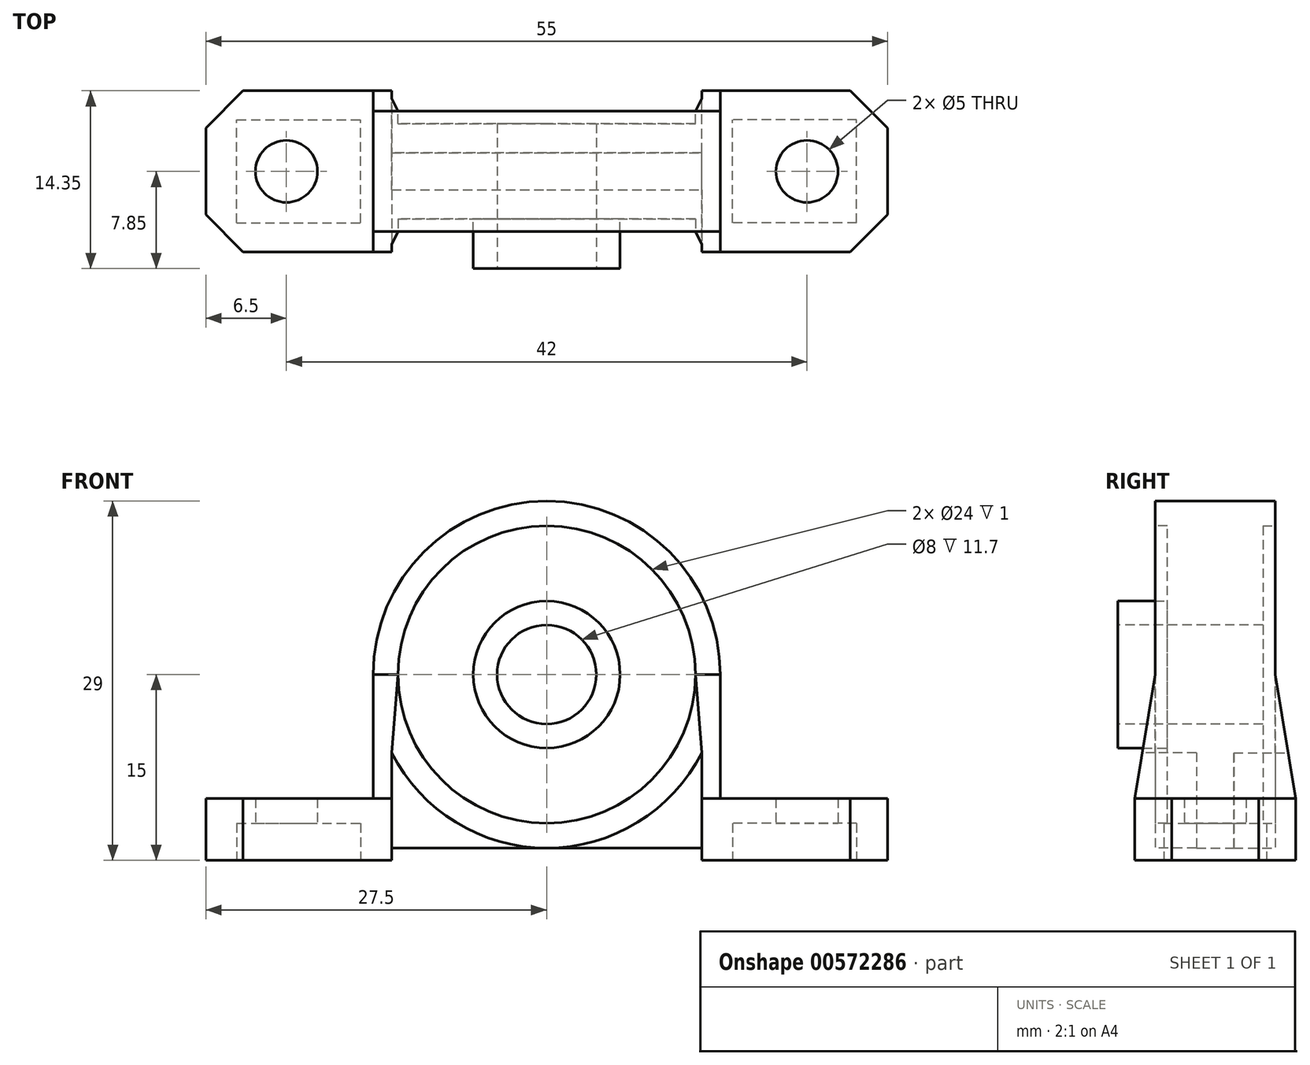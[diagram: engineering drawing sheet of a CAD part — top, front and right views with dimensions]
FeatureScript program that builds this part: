
annotation { "Feature Type Name" : "Feature", "Feature Type Description" : "" }
export const myFeature = defineFeature(function(context is Context, id is Id, definition is map)
    precondition{}
    {
        {
            var Q0;
            Q0=qCreatedBy(makeId("Top.planeOp"),FACE);
            var sketch = newSketch(context, id + "F0", { "sketchPlane" : qUnion([Q0])});
            skLineSegment(sketch, "E0.bottom", {"start": v(-27.5, 6.5) * mm, "end": v(-12.5, 6.5) * mm});
            skLineSegment(sketch, "E0.top", {"start": v(-27.5, -6.5) * mm, "end": v(-12.5, -6.5) * mm});
            skLineSegment(sketch, "E0.left", {"start": v(-27.5, 6.5) * mm, "end": v(-27.5, -6.5) * mm});
            skLineSegment(sketch, "E0.right", {"start": v(-12.5, 6.5) * mm, "end": v(-12.5, -6.5) * mm});
            skCircle(sketch, "E1", {"center": v(-21, 0) * mm, "radius": 2.5 * mm});
            skLineSegment(sketch, "E2.MirrorCS", {"start": v(12.5, 6.5) * mm, "end": v(12.5, -6.5) * mm});
            skLineSegment(sketch, "E3.MirrorCS", {"start": v(27.5, 6.5) * mm, "end": v(12.5, 6.5) * mm});
            skLineSegment(sketch, "E4.MirrorCS", {"start": v(27.5, 6.5) * mm, "end": v(27.5, -6.5) * mm});
            skLineSegment(sketch, "E5.MirrorCS", {"start": v(27.5, -6.5) * mm, "end": v(12.5, -6.5) * mm});
            skCircle(sketch, "E6.MirrorC", {"center": v(21, 0) * mm, "radius": 2.5 * mm});
            skSolve(sketch);
        }
        {
            var Q0;
            Q0 = qSketchRegion(id + "F0", true);
            extrude(context, id + "F1", {"entities" : qUnion([Q0]), "depth" : 5 * mm, "offsetDistance" : 25 * mm});
        }
        {
            var Q0;
            Q0=qCreatedBy(makeId("Top.planeOp"),FACE);
            var sketch = newSketch(context, id + "F2", { "sketchPlane" : qUnion([Q0])});
            skLineSegment(sketch, "E7.bottom", {"start": v(-14, 6.5) * mm, "end": v(14, 6.5) * mm});
            skLineSegment(sketch, "E7.top", {"start": v(-14, -6.5) * mm, "end": v(14, -6.5) * mm});
            skLineSegment(sketch, "E7.left", {"start": v(-14, 6.5) * mm, "end": v(-14, -6.5) * mm});
            skLineSegment(sketch, "E7.right", {"start": v(14, 6.5) * mm, "end": v(14, -6.5) * mm});
            skSolve(sketch);
        }
        {
            var Q0;
            Q0 = qSketchRegion(id + "F2", true);
            extrude(context, id + "F3", {"entities" : qUnion([Q0]), "depth" : 29 * mm, "offsetDistance" : 25 * mm});
        }
        {
            var Q0;
            Q0=makeQuery(id+"F3.opExtrude","SWEPT_FACE",FACE,{"disambiguationData":[OSD([sQuery(id+"F2.wireOp",EDGE,"E7.top")])]});
            var sketch = newSketch(context, id + "F4", { "sketchPlane" : qUnion([Q0])});
            skArc(sketch, "E8", {"start": v(14, 15) * mm, "mid": v(0, 29) * mm, "end": v(-14, 15) * mm});
            skPoint(sketch, "E9.orphan", {"position": v(-18.59, 15) * mm});
            skLineSegment(sketch, "E10", {"start": v(-14, 15) * mm, "end": v(-14, 29) * mm});
            skLineSegment(sketch, "E11", {"start": v(-14, 29) * mm, "end": v(14, 29) * mm});
            skLineSegment(sketch, "E12", {"start": v(14, 29) * mm, "end": v(14, 15) * mm});
            skSolve(sketch);
        }
        {
            var Q0;
            Q0 = qSketchRegion(id + "F4", true);
            extrude(context, id + "F5", {"entities" : qUnion([Q0]), "operationType" : NewBodyOperationType.REMOVE, "endBound" : BoundingType.THROUGH_ALL, "oppositeDirection" : true, "depth" : 25 * mm, "offsetDistance" : 25 * mm});
        }
        {
            var Q0;
            Q0=makeQuery(id+"F3.opExtrude","CAP_FACE",FACE,{"disambiguationData":[OSD([sQuery(id+"F2.wireOp",EDGE,"E7.bottom"),sQuery(id+"F2.wireOp",EDGE,"E7.top"),sQuery(id+"F2.wireOp",EDGE,"E7.left"),sQuery(id+"F2.wireOp",EDGE,"E7.right")])],"isStart":true});
            var sketch = newSketch(context, id + "F6", { "sketchPlane" : qUnion([Q0])});
            skLineSegment(sketch, "E13", {"start": v(-12.5, 1.5) * mm, "end": v(12.5, 1.5) * mm});
            skLineSegment(sketch, "E14", {"start": v(-12.5, -1.5) * mm, "end": v(12.5, -1.5) * mm});
            skLineSegment(sketch, "E15", {"start": v(-12.5, 1.5) * mm, "end": v(-12.5, 6.5) * mm});
            skLineSegment(sketch, "E16", {"start": v(-12.5, 6.5) * mm, "end": v(12.5, 6.5) * mm});
            skLineSegment(sketch, "E17", {"start": v(12.5, 6.5) * mm, "end": v(12.5, 1.5) * mm});
            skLineSegment(sketch, "E18", {"start": v(-12.5, -1.5) * mm, "end": v(-12.5, -6.5) * mm});
            skLineSegment(sketch, "E19", {"start": v(-12.5, -6.5) * mm, "end": v(12.5, -6.5) * mm});
            skLineSegment(sketch, "E20", {"start": v(12.5, -6.5) * mm, "end": v(12.5, -1.5) * mm});
            skSolve(sketch);
        }
        {
            var Q0;
            Q0 = qSketchRegion(id + "F6", true);
            extrude(context, id + "F7", {"entities" : qUnion([Q0]), "operationType" : NewBodyOperationType.REMOVE, "oppositeDirection" : true, "depth" : 1 * mm, "offsetDistance" : 25 * mm});
        }
        {
            var Q0;
            Q0=qCreatedBy(makeId("Right.planeOp"),FACE);
            var sketch = newSketch(context, id + "F8", { "sketchPlane" : qUnion([Q0])});
            skLineSegment(sketch, "E21", {"start": v(-6.5, 5) * mm, "end": v(-4.85, 15) * mm});
            skLineSegment(sketch, "E22", {"start": v(-4.85, 15) * mm, "end": v(-4.85, 29) * mm});
            skLineSegment(sketch, "E23", {"start": v(-4.85, 29) * mm, "end": v(-6.5, 29) * mm});
            skLineSegment(sketch, "E24", {"start": v(-6.5, 29) * mm, "end": v(-6.5, 5) * mm});
            skLineSegment(sketch, "E25.MirrorCS", {"start": v(4.85, 15) * mm, "end": v(4.85, 29) * mm});
            skLineSegment(sketch, "E26.MirrorCS", {"start": v(4.85, 29) * mm, "end": v(6.5, 29) * mm});
            skLineSegment(sketch, "E27.MirrorCS", {"start": v(6.5, 29) * mm, "end": v(6.5, 5) * mm});
            skLineSegment(sketch, "E28.MirrorCS", {"start": v(6.5, 5) * mm, "end": v(4.85, 15) * mm});
            skSolve(sketch);
        }
        {
            var Q0;
            Q0 = qSketchRegion(id + "F8", true);
            extrude(context, id + "F9", {"entities" : qUnion([Q0]), "operationType" : NewBodyOperationType.REMOVE, "oppositeDirection" : true, "depth" : 28 * mm, "offsetDistance" : 25 * mm, "symmetric" : true});
        }
        {
            var Q0;
            Q0=makeQuery(id+"F3.opExtrude","SWEPT_FACE",FACE,{"disambiguationData":[OSD([sQuery(id+"F2.wireOp",EDGE,"E7.top")])]});
            var sketch = newSketch(context, id + "F10", { "sketchPlane" : qUnion([Q0])});
            skCircle(sketch, "E29", {"center": v(0, 15) * mm, "radius": 12 * mm});
            skSolve(sketch);
        }
        {
            var Q0;
            Q0 = qSketchRegion(id + "F10", true);
            extrude(context, id + "F11", {"entities" : qUnion([Q0]), "operationType" : NewBodyOperationType.REMOVE, "oppositeDirection" : true, "depth" : 2.65 * mm, "offsetDistance" : 25 * mm});
        }
        {
            var Q0;
            Q0=makeQuery(id+"F3.opExtrude","SWEPT_FACE",FACE,{"disambiguationData":[OSD([sQuery(id+"F2.wireOp",EDGE,"E7.bottom")])]});
            var sketch = newSketch(context, id + "F12", { "sketchPlane" : qUnion([Q0])});
            skCircle(sketch, "E30", {"center": v(0, 15) * mm, "radius": 12 * mm});
            skSolve(sketch);
        }
        {
            var Q0;
            Q0 = qSketchRegion(id + "F12", true);
            extrude(context, id + "F13", {"entities" : qUnion([Q0]), "operationType" : NewBodyOperationType.REMOVE, "oppositeDirection" : true, "depth" : 2.65 * mm, "offsetDistance" : 25 * mm});
        }
        {
            var Q0;
            Q0=makeQuery(id+"F11.boolean.opBoolean","COPY",FACE,{"derivedFrom":makeQuery(id+"F11.opExtrude","CAP_FACE",FACE,{"disambiguationData":[OSD([sQuery(id+"F10.wireOp",EDGE,"E29")])],"isStart":false})});
            var sketch = newSketch(context, id + "F14", { "sketchPlane" : qUnion([Q0])});
            skCircle(sketch, "E31", {"center": v(0, 15) * mm, "radius": 5.92 * mm});
            skSolve(sketch);
        }
        {
            var Q0;
            Q0 = qSketchRegion(id + "F14", true);
            extrude(context, id + "F15", {"entities" : qUnion([Q0]), "operationType" : NewBodyOperationType.ADD, "depth" : 4 * mm, "offsetDistance" : 25 * mm});
        }
        {
            var Q0;
            Q0=makeQuery(id+"F15.opExtrude","CAP_FACE",FACE,{"disambiguationData":[OSD([sQuery(id+"F14.wireOp",EDGE,"E31")])],"isStart":false});
            var sketch = newSketch(context, id + "F16", { "sketchPlane" : qUnion([Q0])});
            skCircle(sketch, "E32", {"center": v(0, 15) * mm, "radius": 4 * mm});
            skSolve(sketch);
        }
        {
            var Q0;
            Q0 = qSketchRegion(id + "F16", true);
            extrude(context, id + "F17", {"entities" : qUnion([Q0]), "operationType" : NewBodyOperationType.REMOVE, "endBound" : BoundingType.THROUGH_ALL, "oppositeDirection" : true, "depth" : 25 * mm, "offsetDistance" : 25 * mm});
        }
        {
            var Q0;
            Q0=makeQuery(id+"F1.opExtrude","SWEPT_BODY",BODY,{"disambiguationData":[OSD([sQuery(id+"F0.wireOp",EDGE,"E0.bottom"),sQuery(id+"F0.wireOp",EDGE,"E0.top"),sQuery(id+"F0.wireOp",EDGE,"E0.left"),sQuery(id+"F0.wireOp",EDGE,"E0.right"),sQuery(id+"F0.wireOp",EDGE,"E1")])]});
            var Q1;
            Q1=makeQuery(id+"F3.opExtrude","SWEPT_BODY",BODY,{"disambiguationData":[OSD([sQuery(id+"F2.wireOp",EDGE,"E7.bottom"),sQuery(id+"F2.wireOp",EDGE,"E7.top"),sQuery(id+"F2.wireOp",EDGE,"E7.left"),sQuery(id+"F2.wireOp",EDGE,"E7.right")])]});
            var Q2;
            Q2=makeQuery(id+"F1.opExtrude","SWEPT_BODY",BODY,{"disambiguationData":[OSD([sQuery(id+"F0.wireOp",EDGE,"E2.MirrorCS"),sQuery(id+"F0.wireOp",EDGE,"E3.MirrorCS"),sQuery(id+"F0.wireOp",EDGE,"E4.MirrorCS"),sQuery(id+"F0.wireOp",EDGE,"E5.MirrorCS"),sQuery(id+"F0.wireOp",EDGE,"E6.MirrorC")])]});
            booleanBodies(context, id + "F18", {"operationType" : BooleanOperationType.UNION, "tools" : qUnion([Q0, Q1, Q2])});
        }
        {
            var Q0;
            Q0=makeQuery(id+"F1.opExtrude","SWEPT_EDGE",EDGE,{"disambiguationData":[OSD([sQuery(id+"F0.wireOp",EDGE,"E4.MirrorCS"),sQuery(id+"F0.wireOp",EDGE,"E5.MirrorCS")])]});
            var Q1;
            Q1=makeQuery(id+"F1.opExtrude","SWEPT_EDGE",EDGE,{"disambiguationData":[OSD([sQuery(id+"F0.wireOp",EDGE,"E3.MirrorCS"),sQuery(id+"F0.wireOp",EDGE,"E4.MirrorCS")])]});
            var Q2;
            Q2=makeQuery(id+"F1.opExtrude","SWEPT_EDGE",EDGE,{"disambiguationData":[OSD([sQuery(id+"F0.wireOp",EDGE,"E0.top"),sQuery(id+"F0.wireOp",EDGE,"E0.left")])]});
            var Q3;
            Q3=makeQuery(id+"F1.opExtrude","SWEPT_EDGE",EDGE,{"disambiguationData":[OSD([sQuery(id+"F0.wireOp",EDGE,"E0.bottom"),sQuery(id+"F0.wireOp",EDGE,"E0.left")])]});
            chamfer(context, id + "F19", {"entities" : qUnion([Q0, Q1, Q2, Q3]), "width" : 3 * mm, "tangentPropagation" : true});
        }
        {
            var Q0;
            Q0=makeQuery(id+"F18.opBoolean","MERGE",FACE,{"derivedFrom":[makeQuery(id+"F1.opExtrude","SWEPT_FACE",FACE,{"disambiguationData":[OSD([sQuery(id+"F0.wireOp",EDGE,"E0.top")])]}),makeQuery(id+"F1.opExtrude","SWEPT_FACE",FACE,{"disambiguationData":[OSD([sQuery(id+"F0.wireOp",EDGE,"E5.MirrorCS")])]}),makeQuery(id+"F3.opExtrude","SWEPT_FACE",FACE,{"disambiguationData":[OSD([sQuery(id+"F2.wireOp",EDGE,"E7.top")])]})]});
            var sketch = newSketch(context, id + "F20", { "sketchPlane" : qUnion([Q0])});
            skArc(sketch, "E33", {"start": v(-12.5, 8.7) * mm, "mid": v(0, 1) * mm, "end": v(12.5, 8.7) * mm});
            skLineSegment(sketch, "E34.0", {"start": v(-12.5, 1) * mm, "end": v(12.5, 1) * mm});
            skLineSegment(sketch, "E35", {"start": v(-12.5, 1) * mm, "end": v(-12.5, 8.7) * mm});
            skLineSegment(sketch, "E36", {"start": v(12.5, 1) * mm, "end": v(12.5, 8.7) * mm});
            skSolve(sketch);
        }
        {
            var Q0;
            Q0 = qSketchRegion(id + "F20", true);
            extrude(context, id + "F21", {"entities" : qUnion([Q0]), "operationType" : NewBodyOperationType.REMOVE, "oppositeDirection" : true, "depth" : 5 * mm, "offsetDistance" : 25 * mm});
        }
        {
            var Q0;
            Q0=makeQuery(id+"F18.opBoolean","MERGE",FACE,{"derivedFrom":[makeQuery(id+"F1.opExtrude","SWEPT_FACE",FACE,{"disambiguationData":[OSD([sQuery(id+"F0.wireOp",EDGE,"E0.bottom")])]}),makeQuery(id+"F1.opExtrude","SWEPT_FACE",FACE,{"disambiguationData":[OSD([sQuery(id+"F0.wireOp",EDGE,"E3.MirrorCS")])]}),makeQuery(id+"F3.opExtrude","SWEPT_FACE",FACE,{"disambiguationData":[OSD([sQuery(id+"F2.wireOp",EDGE,"E7.bottom")])]})]});
            var sketch = newSketch(context, id + "F22", { "sketchPlane" : qUnion([Q0])});
            skArc(sketch, "E37", {"start": v(-12.5, 8.7) * mm, "mid": v(0, 1) * mm, "end": v(12.5, 8.7) * mm});
            skLineSegment(sketch, "E38.0", {"start": v(12.5, 1) * mm, "end": v(-12.5, 1) * mm});
            skLineSegment(sketch, "E39", {"start": v(-12.5, 1) * mm, "end": v(-12.5, 8.7) * mm});
            skLineSegment(sketch, "E40", {"start": v(12.5, 1) * mm, "end": v(12.5, 8.7) * mm});
            skSolve(sketch);
        }
        {
            var Q0;
            Q0 = qSketchRegion(id + "F22", true);
            extrude(context, id + "F23", {"entities" : qUnion([Q0]), "operationType" : NewBodyOperationType.REMOVE, "oppositeDirection" : true, "depth" : 5 * mm, "offsetDistance" : 25 * mm});
        }
        {
            var Q0;
            Q0=makeQuery(id+"F18.opBoolean","MERGE",FACE,{"derivedFrom":[makeQuery(id+"F1.opExtrude","CAP_FACE",FACE,{"disambiguationData":[OSD([sQuery(id+"F0.wireOp",EDGE,"E0.bottom"),sQuery(id+"F0.wireOp",EDGE,"E0.top"),sQuery(id+"F0.wireOp",EDGE,"E0.left"),sQuery(id+"F0.wireOp",EDGE,"E0.right"),sQuery(id+"F0.wireOp",EDGE,"E1")])],"isStart":true}),makeQuery(id+"F1.opExtrude","CAP_FACE",FACE,{"disambiguationData":[OSD([sQuery(id+"F0.wireOp",EDGE,"E2.MirrorCS"),sQuery(id+"F0.wireOp",EDGE,"E3.MirrorCS"),sQuery(id+"F0.wireOp",EDGE,"E4.MirrorCS"),sQuery(id+"F0.wireOp",EDGE,"E5.MirrorCS"),sQuery(id+"F0.wireOp",EDGE,"E6.MirrorC")])],"isStart":true}),makeQuery(id+"F3.opExtrude","CAP_FACE",FACE,{"disambiguationData":[OSD([sQuery(id+"F2.wireOp",EDGE,"E7.bottom"),sQuery(id+"F2.wireOp",EDGE,"E7.top"),sQuery(id+"F2.wireOp",EDGE,"E7.left"),sQuery(id+"F2.wireOp",EDGE,"E7.right")])],"isStart":true})]});
            var sketch = newSketch(context, id + "F24", { "sketchPlane" : qUnion([Q0])});
            skLineSegment(sketch, "E41.bottom", {"start": v(-12.5, 1.5) * mm, "end": v(12.5, 1.5) * mm});
            skLineSegment(sketch, "E41.top", {"start": v(-12.5, -1.5) * mm, "end": v(12.5, -1.5) * mm});
            skLineSegment(sketch, "E41.left", {"start": v(-12.5, 1.5) * mm, "end": v(-12.5, -1.5) * mm});
            skLineSegment(sketch, "E41.right", {"start": v(12.5, 1.5) * mm, "end": v(12.5, -1.5) * mm});
            skSolve(sketch);
        }
        {
            var Q0;
            Q0 = qSketchRegion(id + "F24", true);
            extrude(context, id + "F25", {"entities" : qUnion([Q0]), "operationType" : NewBodyOperationType.REMOVE, "oppositeDirection" : true, "depth" : 1 * mm, "offsetDistance" : 25 * mm});
        }
        {
            var Q0;
            {var subQ2=makeQuery(id+"F11.opExtrude","SWEPT_FACE",FACE,{"disambiguationData":[OSD([sQuery(id+"F10.wireOp",EDGE,"E29")])]});var subQ4=makeQuery(id+"F3.opExtrude","SWEPT_FACE",FACE,{"disambiguationData":[OSD([sQuery(id+"F2.wireOp",EDGE,"E7.top")])]});var subQ8=sQuery(id+"F0.wireOp",EDGE,"E0.top");Q0=makeQuery(id+"F21.boolean.opBoolean","SPLIT",FACE,{"disambiguationData":[TD([makeQuery(id+"F11.boolean.opBoolean","COPY",FACE,{"derivedFrom":subQ2})])],"derivedFrom":makeQuery(id+"F18.opBoolean","MERGE",FACE,{"derivedFrom":[makeQuery(id+"F1.opExtrude","SWEPT_FACE",FACE,{"disambiguationData":[OSD([subQ8])]}),makeQuery(id+"F1.opExtrude","SWEPT_FACE",FACE,{"disambiguationData":[OSD([sQuery(id+"F0.wireOp",EDGE,"E5.MirrorCS")])]}),subQ4]})});}
            var sketch = newSketch(context, id + "F26", { "sketchPlane" : qUnion([Q0])});
            skArc(sketch, "E42.0", {"start": v(-9.8, 5) * mm, "mid": v(-11.3, 6.74) * mm, "end": v(-12.5, 8.7) * mm});
            skArc(sketch, "E43.0", {"start": v(-9.8, 5) * mm, "mid": v(0, 1) * mm, "end": v(9.8, 5) * mm});
            skArc(sketch, "E44.0", {"start": v(12.5, 8.7) * mm, "mid": v(11.3, 6.74) * mm, "end": v(9.8, 5) * mm});
            skArc(sketch, "E45.0", {"start": v(-6.63, 5) * mm, "mid": v(-10.57, 9.33) * mm, "end": v(-12, 15) * mm});
            skArc(sketch, "E46.0", {"start": v(-6.63, 5) * mm, "mid": v(0, 3) * mm, "end": v(6.63, 5) * mm});
            skArc(sketch, "E47.0", {"start": v(12, 15) * mm, "mid": v(10.57, 9.33) * mm, "end": v(6.63, 5) * mm});
            skLineSegment(sketch, "E48", {"start": v(-12.5, 8.7) * mm, "end": v(-12, 15) * mm});
            skLineSegment(sketch, "E49", {"start": v(12.5, 8.7) * mm, "end": v(12, 15) * mm});
            skSolve(sketch);
        }
        {
            var Q0;
            Q0 = qSketchRegion(id + "F26", true);
            extrude(context, id + "F27", {"entities" : qUnion([Q0]), "operationType" : NewBodyOperationType.REMOVE, "oppositeDirection" : true, "depth" : 1.65 * mm, "offsetDistance" : 25 * mm});
        }
        {
            var Q0;
            {var subQ2=makeQuery(id+"F13.opExtrude","SWEPT_FACE",FACE,{"disambiguationData":[OSD([sQuery(id+"F12.wireOp",EDGE,"E30")])]});var subQ4=makeQuery(id+"F3.opExtrude","SWEPT_FACE",FACE,{"disambiguationData":[OSD([sQuery(id+"F2.wireOp",EDGE,"E7.bottom")])]});var subQ6=sQuery(id+"F0.wireOp",EDGE,"E0.bottom");Q0=makeQuery(id+"F23.boolean.opBoolean","SPLIT",FACE,{"disambiguationData":[TD([makeQuery(id+"F13.boolean.opBoolean","COPY",FACE,{"derivedFrom":subQ2})])],"derivedFrom":makeQuery(id+"F18.opBoolean","MERGE",FACE,{"derivedFrom":[makeQuery(id+"F1.opExtrude","SWEPT_FACE",FACE,{"disambiguationData":[OSD([subQ6])]}),makeQuery(id+"F1.opExtrude","SWEPT_FACE",FACE,{"disambiguationData":[OSD([sQuery(id+"F0.wireOp",EDGE,"E3.MirrorCS")])]}),subQ4]})});}
            var sketch = newSketch(context, id + "F28", { "sketchPlane" : qUnion([Q0])});
            skArc(sketch, "E50.0", {"start": v(-12.5, 8.7) * mm, "mid": v(-11.3, 6.74) * mm, "end": v(-9.8, 5) * mm});
            skArc(sketch, "E51.0", {"start": v(-9.8, 5) * mm, "mid": v(0, 1) * mm, "end": v(9.8, 5) * mm});
            skArc(sketch, "E52.0", {"start": v(9.8, 5) * mm, "mid": v(11.3, 6.74) * mm, "end": v(12.5, 8.7) * mm});
            skArc(sketch, "E53.0", {"start": v(6.63, 5) * mm, "mid": v(10.57, 9.33) * mm, "end": v(12, 15) * mm});
            skArc(sketch, "E54.0", {"start": v(-6.63, 5) * mm, "mid": v(0, 3) * mm, "end": v(6.63, 5) * mm});
            skArc(sketch, "E55.0", {"start": v(-12, 15) * mm, "mid": v(-10.57, 9.33) * mm, "end": v(-6.63, 5) * mm});
            skLineSegment(sketch, "E56", {"start": v(-12.5, 8.7) * mm, "end": v(-12, 15) * mm});
            skLineSegment(sketch, "E57", {"start": v(12, 15) * mm, "end": v(12.5, 8.7) * mm});
            skSolve(sketch);
        }
        {
            var Q0;
            Q0 = qSketchRegion(id + "F28", true);
            extrude(context, id + "F29", {"entities" : qUnion([Q0]), "operationType" : NewBodyOperationType.REMOVE, "oppositeDirection" : true, "depth" : 1.65 * mm, "offsetDistance" : 25 * mm});
        }
        {
            var Q0;
            {var subQ0=sQuery(id+"F2.wireOp",EDGE,"E7.bottom");var subQ1=sQuery(id+"F0.wireOp",EDGE,"E0.left");var subQ2=sQuery(id+"F0.wireOp",EDGE,"E5.MirrorCS");var subQ3=sQuery(id+"F0.wireOp",EDGE,"E3.MirrorCS");var subQ4=sQuery(id+"F0.wireOp",EDGE,"E1");var subQ5=sQuery(id+"F0.wireOp",EDGE,"E0.bottom");var subQ6=sQuery(id+"F0.wireOp",EDGE,"E0.right");var subQ7=sQuery(id+"F0.wireOp",EDGE,"E0.top");var subQ8=sQuery(id+"F2.wireOp",EDGE,"E7.top");Q0=makeQuery(id+"F25.boolean.opBoolean","SPLIT",FACE,{"disambiguationData":[TD([makeQuery(id+"F1.opExtrude","SWEPT_FACE",FACE,{"disambiguationData":[OSD([subQ1])]})])],"derivedFrom":makeQuery(id+"F18.opBoolean","MERGE",FACE,{"derivedFrom":[makeQuery(id+"F1.opExtrude","CAP_FACE",FACE,{"disambiguationData":[OSD([subQ5,subQ7,subQ1,subQ6,subQ4])],"isStart":true}),makeQuery(id+"F1.opExtrude","CAP_FACE",FACE,{"disambiguationData":[OSD([sQuery(id+"F0.wireOp",EDGE,"E2.MirrorCS"),subQ3,sQuery(id+"F0.wireOp",EDGE,"E4.MirrorCS"),subQ2,sQuery(id+"F0.wireOp",EDGE,"E6.MirrorC")])],"isStart":true}),makeQuery(id+"F3.opExtrude","CAP_FACE",FACE,{"disambiguationData":[OSD([subQ0,subQ8,sQuery(id+"F2.wireOp",EDGE,"E7.left"),sQuery(id+"F2.wireOp",EDGE,"E7.right")])],"isStart":true})]})});}
            var sketch = newSketch(context, id + "F30", { "sketchPlane" : qUnion([Q0])});
            skLineSegment(sketch, "E58.bottom", {"start": v(-25, 4.15) * mm, "end": v(-15, 4.15) * mm});
            skLineSegment(sketch, "E58.top", {"start": v(-25, -4.15) * mm, "end": v(-15, -4.15) * mm});
            skLineSegment(sketch, "E58.left", {"start": v(-25, 4.15) * mm, "end": v(-25, -4.15) * mm});
            skLineSegment(sketch, "E58.right", {"start": v(-15, 4.15) * mm, "end": v(-15, -4.15) * mm});
            skLineSegment(sketch, "E59.MirrorCS", {"start": v(15, 4.15) * mm, "end": v(15, -4.15) * mm});
            skLineSegment(sketch, "E60.MirrorCS", {"start": v(25, 4.15) * mm, "end": v(15, 4.15) * mm});
            skLineSegment(sketch, "E61.MirrorCS", {"start": v(25, 4.15) * mm, "end": v(25, -4.15) * mm});
            skLineSegment(sketch, "E62.MirrorCS", {"start": v(25, -4.15) * mm, "end": v(15, -4.15) * mm});
            skSolve(sketch);
        }
        {
            var Q0;
            Q0 = qSketchRegion(id + "F30", true);
            extrude(context, id + "F31", {"entities" : qUnion([Q0]), "operationType" : NewBodyOperationType.REMOVE, "oppositeDirection" : true, "depth" : 3 * mm, "offsetDistance" : 25 * mm});
        }
    });
